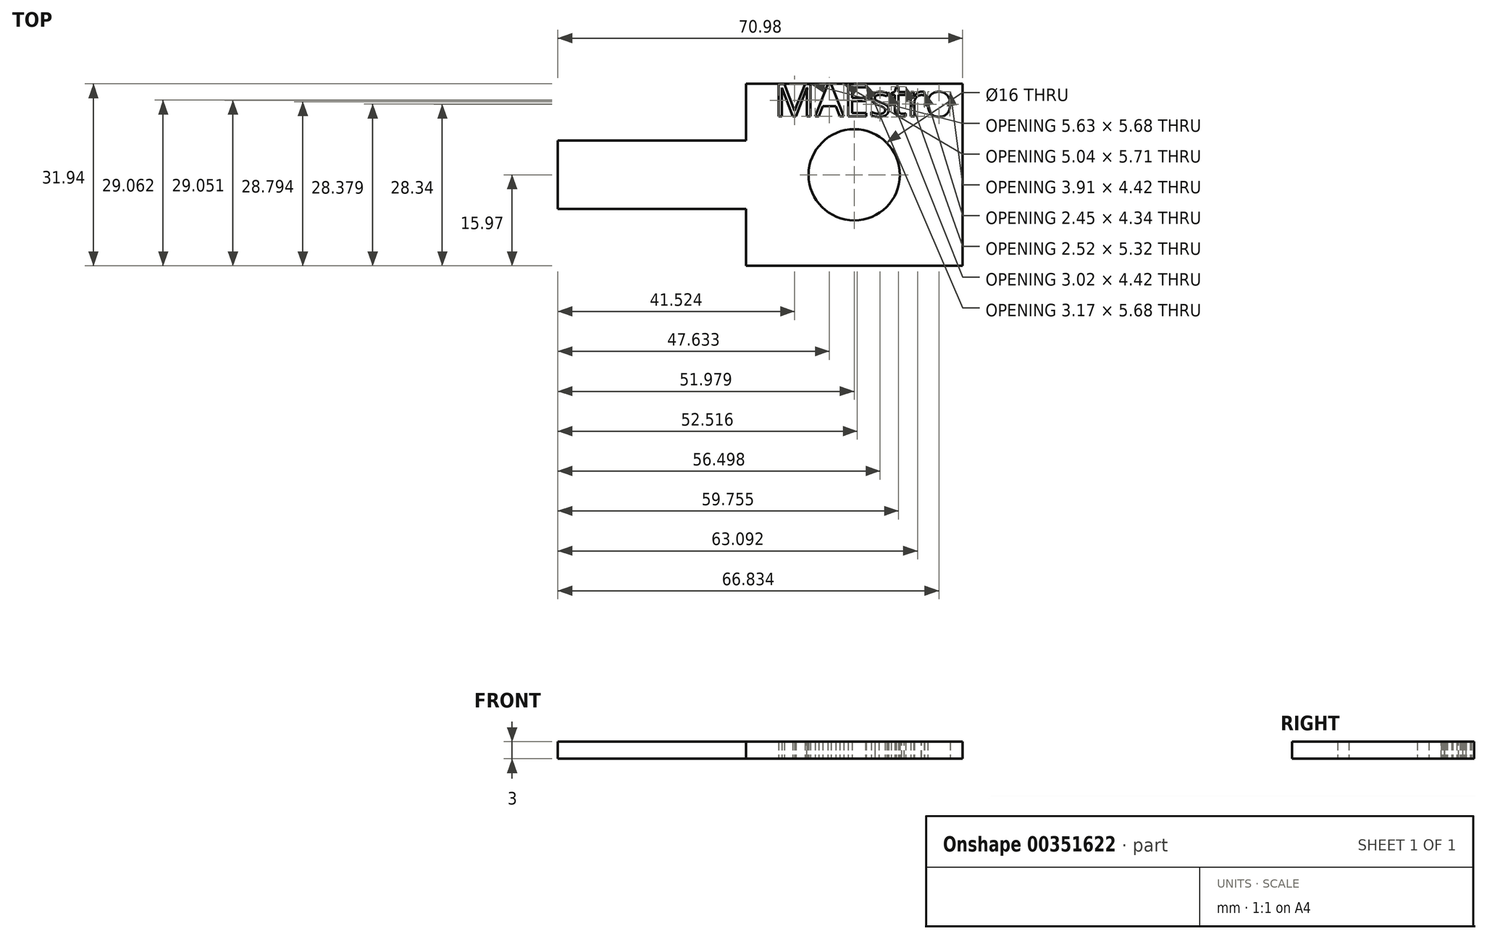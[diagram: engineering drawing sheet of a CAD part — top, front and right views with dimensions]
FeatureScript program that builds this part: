
annotation { "Feature Type Name" : "Feature", "Feature Type Description" : "" }
export const myFeature = defineFeature(function(context is Context, id is Id, definition is map)
    precondition{}
    {
        {
            var Q0;
            Q0=qCreatedBy(makeId("Top.planeOp"),FACE);
            var sketch = newSketch(context, id + "F0", { "sketchPlane" : qUnion([Q0])});
            skLineSegment(sketch, "E0.bottom", {"start": v(18, 6) * mm, "end": v(-18, 6) * mm});
            skLineSegment(sketch, "E0.top", {"start": v(18, -6) * mm, "end": v(-18, -6) * mm});
            skLineSegment(sketch, "E0.left", {"start": v(18, 6) * mm, "end": v(18, -6) * mm});
            skLineSegment(sketch, "E0.right", {"start": v(-18, 6) * mm, "end": v(-18, -6) * mm});
            skPoint(sketch, "E0.middle", {"position": v(0, 0) * mm});
            skLineSegment(sketch, "E1.bottom", {"start": v(14.98, 15.97) * mm, "end": v(52.98, 15.97) * mm});
            skLineSegment(sketch, "E1.top", {"start": v(14.98, -15.97) * mm, "end": v(52.98, -15.97) * mm});
            skLineSegment(sketch, "E1.left", {"start": v(14.98, 15.97) * mm, "end": v(14.98, -15.97) * mm});
            skLineSegment(sketch, "E1.right", {"start": v(52.98, 15.97) * mm, "end": v(52.98, -15.97) * mm});
            skPoint(sketch, "E1.middle", {"position": v(33.98, 0) * mm});
            skCircle(sketch, "E2", {"center": v(33.98, 0) * mm, "radius": 8 * mm});
            skText(sketch, "E3", { "text": "MAEstro", "fontName": "OpenSans-Regular.ttf"});
            const initialGuessF0  = {"E3": [0.01993, 0.01024, 1, 0, 0.00573]};
            skSetInitialGuess(sketch, initialGuessF0);
            skSolve(sketch);
        }
        {
            var Q0;
            Q0=makeQuery(id+"F0.imprint","IMPRINT",FACE,{"disambiguationData":[TD([[makeQuery(id+"F0.imprint","IMPRINT",EDGE,{"derivedFrom":sQuery(id+"F0.wireOp",EDGE,"E1.bottom")}),-1.0]])]});
            var Q1;
            Q1=makeQuery(id+"F0.imprint","IMPRINT",FACE,{"disambiguationData":[TD([[makeQuery(id+"F0.imprint","IMPRINT",EDGE,{"derivedFrom":sQuery(id+"F0.wireOp",EDGE,"E0.bottom")}),1.0]])]});
            extrude(context, id + "F1", {"entities" : qUnion([Q0, Q1]), "depth" : 3 * mm});
        }
    });
